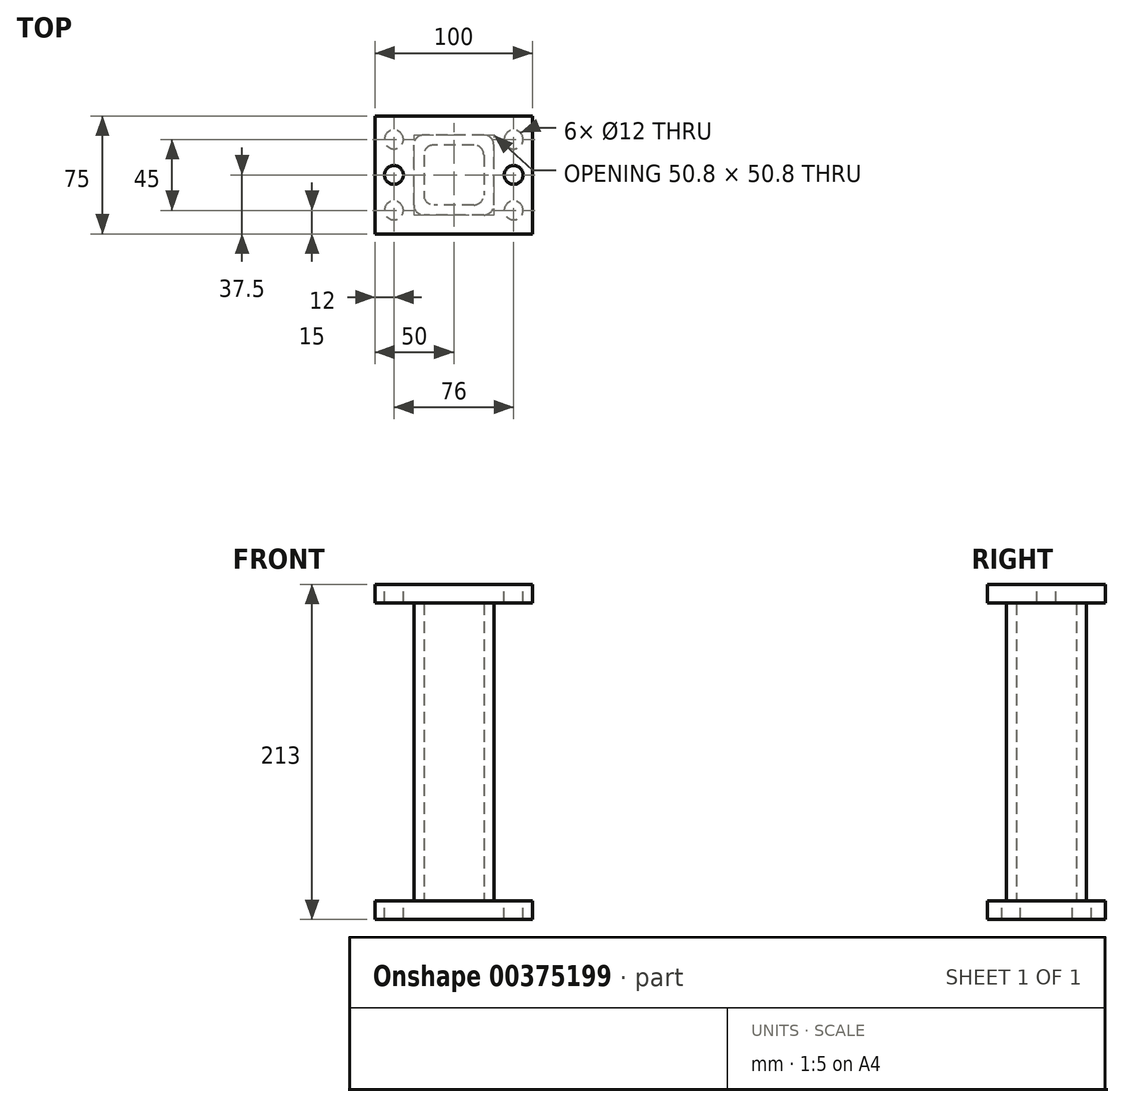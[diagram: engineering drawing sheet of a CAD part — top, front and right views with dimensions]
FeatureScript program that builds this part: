
annotation { "Feature Type Name" : "Feature", "Feature Type Description" : "" }
export const myFeature = defineFeature(function(context is Context, id is Id, definition is map)
    precondition{}
    {
        {
            var Q0;
            Q0=qCreatedBy(makeId("Top.planeOp"),FACE);
            var sketch = newSketch(context, id + "F0", { "sketchPlane" : qUnion([Q0])});
            skLineSegment(sketch, "E0.bottom", {"start": v(50, 37.5) * mm, "end": v(-50, 37.5) * mm});
            skLineSegment(sketch, "E0.top", {"start": v(50, -37.5) * mm, "end": v(-50, -37.5) * mm});
            skLineSegment(sketch, "E0.left", {"start": v(50, 37.5) * mm, "end": v(50, -37.5) * mm});
            skLineSegment(sketch, "E0.right", {"start": v(-50, 37.5) * mm, "end": v(-50, -37.5) * mm});
            skPoint(sketch, "E0.middle", {"position": v(0, 0) * mm});
            skSolve(sketch);
        }
        {
            var Q0;
            Q0=makeQuery(id+"F0.imprint","IMPRINT",FACE,{"disambiguationData":[TD([[makeQuery(id+"F0.imprint","IMPRINT",EDGE,{"derivedFrom":sQuery(id+"F0.wireOp",EDGE,"E0.bottom")}),1.0]])]});
            extrude(context, id + "F1", {"entities" : qUnion([Q0]), "depth" : -12 * mm});
        }
        {
            var Q0;
            Q0=makeQuery(id+"F1.opExtrude","CAP_FACE",FACE,{"disambiguationData":[OSD([sQuery(id+"F0.wireOp",EDGE,"E0.bottom"),sQuery(id+"F0.wireOp",EDGE,"E0.top"),sQuery(id+"F0.wireOp",EDGE,"E0.left"),sQuery(id+"F0.wireOp",EDGE,"E0.right")])],"isStart":true});
            var sketch = newSketch(context, id + "F2", { "sketchPlane" : qUnion([Q0])});
            skLineSegment(sketch, "E1.bottom", {"start": v(19.05, -25.4) * mm, "end": v(-19.05, -25.4) * mm});
            skLineSegment(sketch, "E1.top", {"start": v(19.05, 25.4) * mm, "end": v(-19.05, 25.4) * mm});
            skLineSegment(sketch, "E1.left", {"start": v(25.4, -19.05) * mm, "end": v(25.4, 19.05) * mm});
            skLineSegment(sketch, "E1.right", {"start": v(-25.4, -19.05) * mm, "end": v(-25.4, 19.05) * mm});
            skPoint(sketch, "E1.middle", {"position": v(0, 0) * mm});
            skPoint(sketch, "E2.visualSharp", {"position": v(-25.4, -25.4) * mm});
            skArc(sketch, "E2.filletArc", {"start": v(-25.4, -19.05) * mm, "mid": v(-23.54, -23.54) * mm, "end": v(-19.05, -25.4) * mm});
            skPoint(sketch, "E3.visualSharp", {"position": v(-25.4, 25.4) * mm});
            skArc(sketch, "E3.filletArc", {"start": v(-19.05, 25.4) * mm, "mid": v(-23.54, 23.54) * mm, "end": v(-25.4, 19.05) * mm});
            skPoint(sketch, "E4.visualSharp", {"position": v(25.4, 25.4) * mm});
            skArc(sketch, "E4.filletArc", {"start": v(25.4, 19.05) * mm, "mid": v(23.54, 23.54) * mm, "end": v(19.05, 25.4) * mm});
            skPoint(sketch, "E5.visualSharp", {"position": v(25.4, -25.4) * mm});
            skArc(sketch, "E5.filletArc", {"start": v(19.05, -25.4) * mm, "mid": v(23.54, -23.54) * mm, "end": v(25.4, -19.05) * mm});
            skLineSegment(sketch, "E6.bottom", {"start": v(12.7, 19.05) * mm, "end": v(-12.7, 19.05) * mm});
            skLineSegment(sketch, "E6.top", {"start": v(12.7, -19.05) * mm, "end": v(-12.7, -19.05) * mm});
            skLineSegment(sketch, "E6.left", {"start": v(19.05, 12.7) * mm, "end": v(19.05, -12.7) * mm});
            skLineSegment(sketch, "E6.right", {"start": v(-19.05, 12.7) * mm, "end": v(-19.05, -12.7) * mm});
            skArc(sketch, "E7.filletArc", {"start": v(-12.7, 19.05) * mm, "mid": v(-17.2, 17.2) * mm, "end": v(-19.05, 12.7) * mm});
            skArc(sketch, "E8.filletArc", {"start": v(19.05, 12.7) * mm, "mid": v(17.2, 17.2) * mm, "end": v(12.7, 19.05) * mm});
            skArc(sketch, "E9.filletArc", {"start": v(12.7, -19.05) * mm, "mid": v(17.2, -17.2) * mm, "end": v(19.05, -12.7) * mm});
            skArc(sketch, "E10.filletArc", {"start": v(-19.05, -12.7) * mm, "mid": v(-17.2, -17.2) * mm, "end": v(-12.7, -19.05) * mm});
            skSolve(sketch);
        }
        {
            var Q0;
            Q0=qSketchRegion(id+"F2",true);
            extrude(context, id + "F3", {"entities" : qUnion([Q0]), "operationType" : NewBodyOperationType.ADD, "depth" : 189 * mm});
        }
        {
            var Q0;
            {var subQ0=sQuery(id+"F0.wireOp",EDGE,"E0.left");var subQ1=sQuery(id+"F0.wireOp",EDGE,"E0.bottom");var subQ2=sQuery(id+"F0.wireOp",EDGE,"E0.right");var subQ3=sQuery(id+"F0.wireOp",EDGE,"E0.top");Q0=makeQuery(id+"F3.boolean.opBoolean","SPLIT",FACE,{"disambiguationData":[TD([makeQuery(id+"F1.opExtrude","SWEPT_FACE",FACE,{"disambiguationData":[OSD([subQ1])]})])],"derivedFrom":makeQuery(id+"F1.opExtrude","CAP_FACE",FACE,{"disambiguationData":[OSD([subQ1,subQ3,subQ0,subQ2])],"isStart":true})});}
            var sketch = newSketch(context, id + "F4", { "sketchPlane" : qUnion([Q0])});
            skLineSegment(sketch, "E11", {"start": v(-50, -37.5) * mm, "end": v(-38, -37.5) * mm, "construction": true});
            skLineSegment(sketch, "E12", {"start": v(-38, -37.5) * mm, "end": v(-38, -22.5) * mm, "construction": true});
            skLineSegment(sketch, "E13", {"start": v(-50, 37.5) * mm, "end": v(-38, 37.5) * mm, "construction": true});
            skLineSegment(sketch, "E14", {"start": v(-38, 37.5) * mm, "end": v(-38, 22.5) * mm, "construction": true});
            skLineSegment(sketch, "E15", {"start": v(50, 37.5) * mm, "end": v(38, 37.5) * mm, "construction": true});
            skLineSegment(sketch, "E16", {"start": v(50, -37.5) * mm, "end": v(38, -37.5) * mm, "construction": true});
            skLineSegment(sketch, "E17", {"start": v(38, -37.5) * mm, "end": v(38, -22.5) * mm, "construction": true});
            skLineSegment(sketch, "E18", {"start": v(38, 37.5) * mm, "end": v(38, 22.5) * mm, "construction": true});
            skSolve(sketch);
        }
        {
            var Q0;
            Q0=makeQuery(id+"F3.opExtrude","CAP_FACE",FACE,{"disambiguationData":[OSD([sQuery(id+"F2.wireOp",EDGE,"E1.bottom"),sQuery(id+"F2.wireOp",EDGE,"E1.top"),sQuery(id+"F2.wireOp",EDGE,"E1.left"),sQuery(id+"F2.wireOp",EDGE,"E1.right"),sQuery(id+"F2.wireOp",EDGE,"E2.filletArc"),sQuery(id+"F2.wireOp",EDGE,"E3.filletArc"),sQuery(id+"F2.wireOp",EDGE,"E4.filletArc"),sQuery(id+"F2.wireOp",EDGE,"E5.filletArc"),sQuery(id+"F2.wireOp",EDGE,"E6.bottom"),sQuery(id+"F2.wireOp",EDGE,"E6.top"),sQuery(id+"F2.wireOp",EDGE,"E6.left"),sQuery(id+"F2.wireOp",EDGE,"E6.right"),sQuery(id+"F2.wireOp",EDGE,"E7.filletArc"),sQuery(id+"F2.wireOp",EDGE,"E8.filletArc"),sQuery(id+"F2.wireOp",EDGE,"E9.filletArc"),sQuery(id+"F2.wireOp",EDGE,"E10.filletArc")])],"isStart":false});
            var sketch = newSketch(context, id + "F5", { "sketchPlane" : qUnion([Q0])});
            skLineSegment(sketch, "E19.bottom", {"start": v(50, -37.5) * mm, "end": v(-50, -37.5) * mm});
            skLineSegment(sketch, "E19.top", {"start": v(50, 37.5) * mm, "end": v(-50, 37.5) * mm});
            skLineSegment(sketch, "E19.left", {"start": v(50, -37.5) * mm, "end": v(50, 37.5) * mm});
            skLineSegment(sketch, "E19.right", {"start": v(-50, -37.5) * mm, "end": v(-50, 37.5) * mm});
            skPoint(sketch, "E19.middle", {"position": v(0, 0) * mm});
            skSolve(sketch);
        }
        {
            var Q0;
            Q0=makeQuery(id+"F5.imprint","IMPRINT",FACE,{"disambiguationData":[TD([[makeQuery(id+"F5.imprint","IMPRINT",EDGE,{"derivedFrom":makeQuery(id+"F3.opExtrude","CAP_EDGE",EDGE,{"disambiguationData":[OSD([sQuery(id+"F2.wireOp",EDGE,"E6.bottom")])],"isStart":false})}),1.0]])]});
            var Q1;
            Q1=makeQuery(id+"F5.imprint","IMPRINT",FACE,{"disambiguationData":[TD([[makeQuery(id+"F5.imprint","IMPRINT",EDGE,{"derivedFrom":sQuery(id+"F5.wireOp",EDGE,"E19.bottom")}),-1.0]])]});
            var Q2;
            Q2=makeQuery(id+"F5.imprint","IMPRINT",FACE,{"disambiguationData":[TD([[makeQuery(id+"F5.imprint","IMPRINT",EDGE,{"derivedFrom":makeQuery(id+"F3.opExtrude","CAP_EDGE",EDGE,{"disambiguationData":[OSD([sQuery(id+"F2.wireOp",EDGE,"E1.bottom")])],"isStart":false})}),-1.0]])]});
            extrude(context, id + "F6", {"entities" : qUnion([Q0, Q1, Q2]), "operationType" : NewBodyOperationType.ADD, "depth" : 12 * mm});
        }
        {
            var Q0;
            Q0=makeQuery(id+"F6.opExtrude","CAP_FACE",FACE,{"disambiguationData":[OSD([sQuery(id+"F5.wireOp",EDGE,"E19.bottom"),sQuery(id+"F5.wireOp",EDGE,"E19.top"),sQuery(id+"F5.wireOp",EDGE,"E19.left"),sQuery(id+"F5.wireOp",EDGE,"E19.right")])],"isStart":false});
            var sketch = newSketch(context, id + "F7", { "sketchPlane" : qUnion([Q0])});
            skLineSegment(sketch, "E20", {"start": v(-50, 0) * mm, "end": v(-38, 0) * mm, "construction": true});
            skLineSegment(sketch, "E21", {"start": v(50, 0) * mm, "end": v(38, 0) * mm, "construction": true});
            skPoint(sketch, "E21.endSnap0", {"position": v(50, 0) * mm});
            skSolve(sketch);
        }
        {
            var Q0;
            Q0=sQuery(id+"F7.wireOp",VERTEX,"E20.end");
            var Q1;
            Q1=sQuery(id+"F7.wireOp",VERTEX,"E21.end");
            var Q2;
            Q2=makeQuery(id+"F1.opExtrude","SWEPT_BODY",BODY,{"disambiguationData":[OSD([sQuery(id+"F0.wireOp",EDGE,"E0.bottom"),sQuery(id+"F0.wireOp",EDGE,"E0.top"),sQuery(id+"F0.wireOp",EDGE,"E0.left"),sQuery(id+"F0.wireOp",EDGE,"E0.right")])]});
            hole(context, id + "F8", {"style" : HoleStyle.SIMPLE, "endStyle" : HoleEndStyle.BLIND, "holeDiameter" : 12 * mm, "holeDepth" : 12 * mm, "isTappedThrough" : true, "tappedDepth" : 12 * mm, "tapClearance" : 3, "locations" : qUnion([Q0, Q1]), "scope" : qUnion([Q2])});
        }
        {
            var Q0;
            Q0=sQuery(id+"F4.wireOp",VERTEX,"E14.end");
            var Q1;
            Q1=sQuery(id+"F4.wireOp",VERTEX,"E18.end");
            var Q2;
            Q2=sQuery(id+"F4.wireOp",VERTEX,"E17.end");
            var Q3;
            Q3=sQuery(id+"F4.wireOp",VERTEX,"E12.end");
            var Q4;
            Q4=makeQuery(id+"F1.opExtrude","SWEPT_BODY",BODY,{"disambiguationData":[OSD([sQuery(id+"F0.wireOp",EDGE,"E0.bottom"),sQuery(id+"F0.wireOp",EDGE,"E0.top"),sQuery(id+"F0.wireOp",EDGE,"E0.left"),sQuery(id+"F0.wireOp",EDGE,"E0.right")])]});
            hole(context, id + "F9", {"style" : HoleStyle.SIMPLE, "endStyle" : HoleEndStyle.BLIND, "holeDiameter" : 12 * mm, "holeDepth" : 12 * mm, "isTappedThrough" : true, "tappedDepth" : 12 * mm, "tapClearance" : 3, "locations" : qUnion([Q0, Q1, Q2, Q3]), "scope" : qUnion([Q4])});
        }
    });
